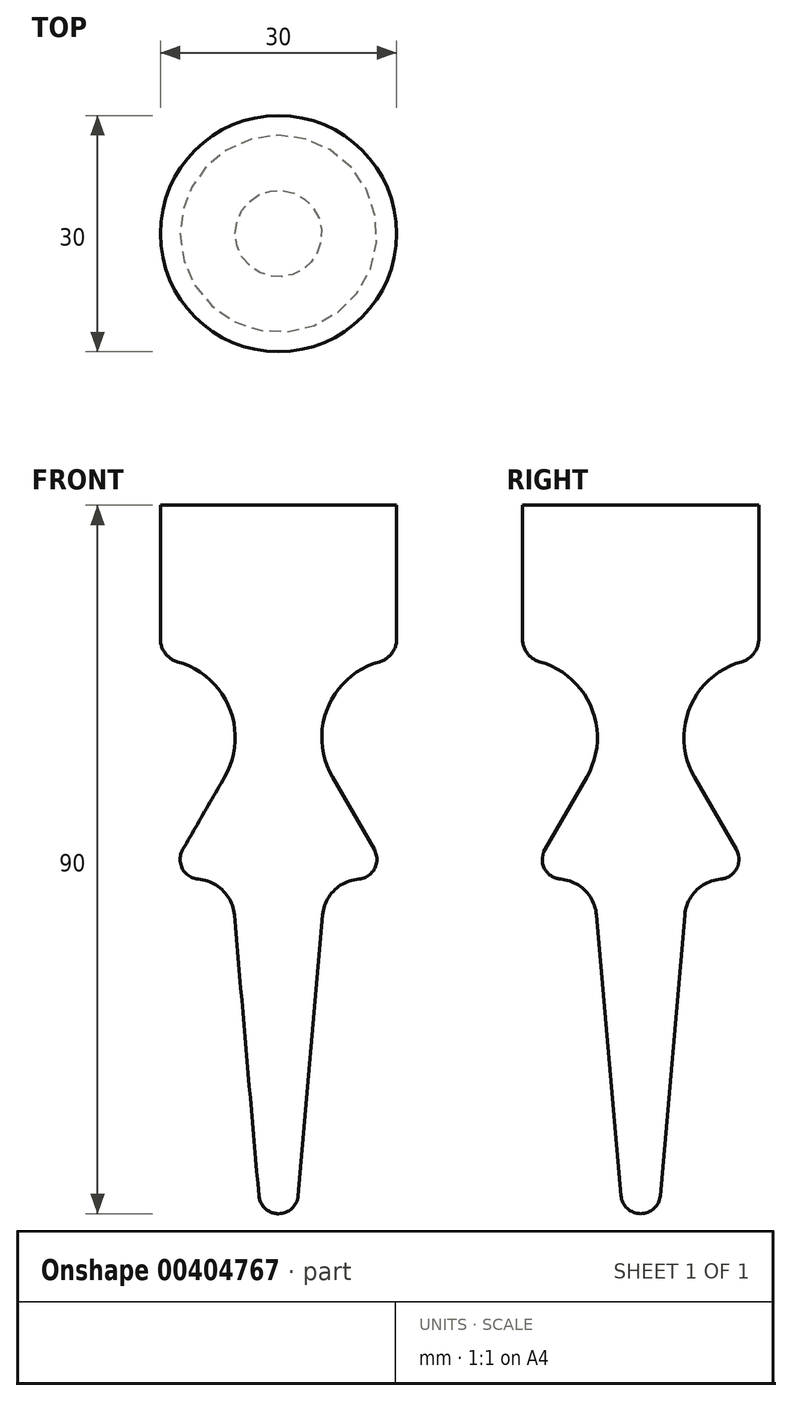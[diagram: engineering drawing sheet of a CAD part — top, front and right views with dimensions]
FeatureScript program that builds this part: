
annotation { "Feature Type Name" : "Feature", "Feature Type Description" : "" }
export const myFeature = defineFeature(function(context is Context, id is Id, definition is map)
    precondition{}
    {
        {
            var Q0;
            Q0=qCreatedBy(makeId("Front.planeOp"),FACE);
            var sketch = newSketch(context, id + "F0", { "sketchPlane" : qUnion([Q0])});
            skLineSegment(sketch, "E0", {"start": v(-2.5, 2.28) * mm, "end": v(-5.61, 37.96) * mm});
            skArc(sketch, "E1", {"start": v(-12.17, 46.25) * mm, "mid": v(-12.21, 43.84) * mm, "end": v(-10.2, 42.5) * mm});
            skArc(sketch, "E2", {"start": v(-5.61, 37.96) * mm, "mid": v(-7.07, 41.07) * mm, "end": v(-10.2, 42.5) * mm});
            skArc(sketch, "E3", {"start": v(-2.5, 2.28) * mm, "mid": v(-1.69, 0.66) * mm, "end": v(0, 0) * mm});
            skLineSegment(sketch, "E4", {"start": v(-12.17, 46.25) * mm, "end": v(-6.84, 55.48) * mm});
            skLineSegment(sketch, "E5", {"start": v(0, 90) * mm, "end": v(-15, 90) * mm});
            skLineSegment(sketch, "E6", {"start": v(-15, 90) * mm, "end": v(-15, 73) * mm});
            skArc(sketch, "E7", {"start": v(-15, 73) * mm, "mid": v(-14.39, 71.19) * mm, "end": v(-12.8, 70.11) * mm});
            skArc(sketch, "E8", {"start": v(-6.84, 55.48) * mm, "mid": v(-6.24, 64.26) * mm, "end": v(-12.8, 70.11) * mm});
            skLineSegment(sketch, "E9", {"start": v(0, 90) * mm, "end": v(0, 0) * mm, "construction": true});
            skSolve(sketch);
        }
        {
            var Q0;
            Q0=sQuery(id+"F0.wireOp",EDGE,"E8");
            var Q1;
            Q1=sQuery(id+"F0.wireOp",EDGE,"E7");
            var Q2;
            Q2=sQuery(id+"F0.wireOp",EDGE,"E6");
            var Q3;
            Q3=sQuery(id+"F0.wireOp",EDGE,"E5");
            var Q4;
            Q4=sQuery(id+"F0.wireOp",EDGE,"E4");
            var Q5;
            Q5=sQuery(id+"F0.wireOp",EDGE,"E3");
            var Q6;
            Q6=sQuery(id+"F0.wireOp",EDGE,"E2");
            var Q7;
            Q7=sQuery(id+"F0.wireOp",EDGE,"E1");
            var Q8;
            Q8=sQuery(id+"F0.wireOp",EDGE,"E0");
            var Q9;
            Q9=sQuery(id+"F0.wireOp",EDGE,"E9");
            revolve(context, id + "F1", {"bodyType" : ToolBodyType.SURFACE, "surfaceEntities" : qUnion([Q0, Q1, Q2, Q3, Q4, Q5, Q6, Q7, Q8]), "axis" : qUnion([Q9]), "revolveType" : RevolveType.FULL});
        }
    });
